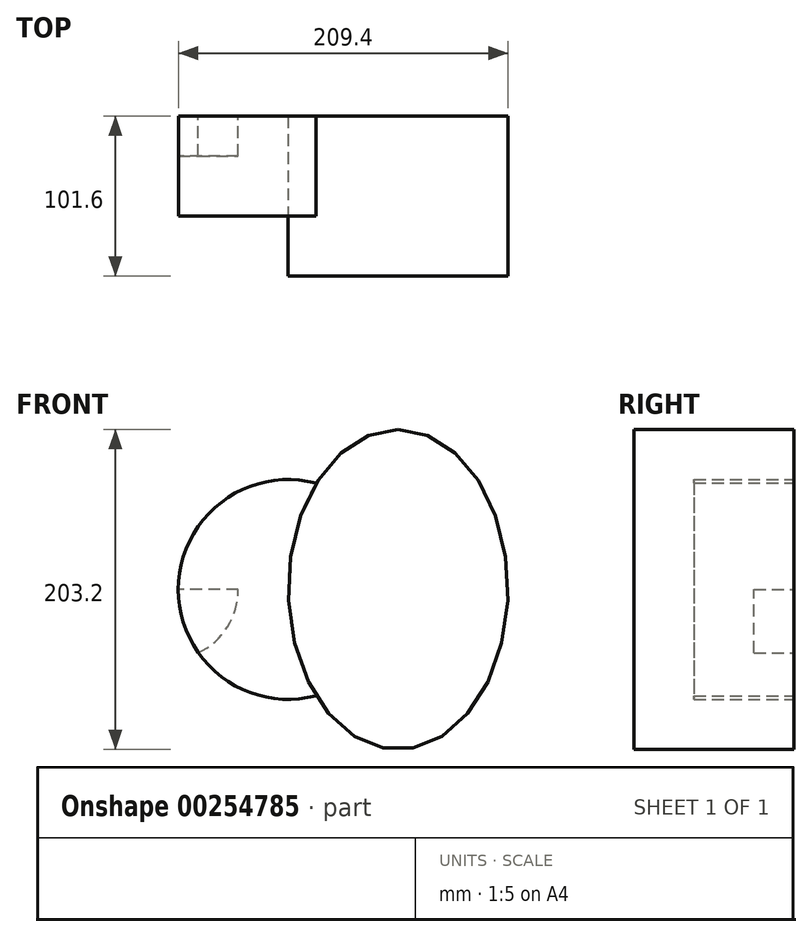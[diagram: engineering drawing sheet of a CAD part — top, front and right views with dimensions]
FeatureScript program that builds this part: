
annotation { "Feature Type Name" : "Feature", "Feature Type Description" : "" }
export const myFeature = defineFeature(function(context is Context, id is Id, definition is map)
    precondition{}
    {
        {
            var Q0;
            Q0=qCreatedBy(makeId("Front.planeOp"),FACE);
            var sketch = newSketch(context, id + "F0", { "sketchPlane" : qUnion([Q0])});
            skLineSegment(sketch, "E0", {"start": v(0, 0) * mm, "end": v(-76.2, 0) * mm});
            skCircle(sketch, "E1", {"center": v(-76.2, 0) * mm, "radius": 44.45 * mm});
            skLineSegment(sketch, "E2", {"start": v(-31.75, 0) * mm, "end": v(-69.85, 0) * mm});
            skCircle(sketch, "E3", {"center": v(0, 0) * mm, "radius": 69.8 * mm});
            skLineSegment(sketch, "E4", {"start": v(69.8, 0) * mm, "end": v(69.8, 101.6) * mm});
            skEllipse(sketch, "E5", {"center": v(69.8, 0) * mm, "majorRadius": 101.6 * mm, "minorRadius": 69.8 * mm, "majorAxis": v(0, 1)});
            skSolve(sketch);
        }
        {
            var Q0;
            {var subQ0=sQuery(id+"F0.wireOp",EDGE,"E3");var subQ1=sQuery(id+"F0.wireOp",EDGE,"E1");var subQ2=makeQuery(id+"F0.imprint","INTERSECT",VERTEX,{"disambiguationData":[OD(0.0)],"derivedFrom":[subQ1,subQ0]});Q0=makeQuery(id+"F0.imprint","IMPRINT",FACE,{"disambiguationData":[TD([[makeQuery(id+"F0.imprint","IMPRINT",EDGE,{"disambiguationData":[TD([[subQ2,-1.0]])],"derivedFrom":subQ1}),1.0]])]});}
            extrude(context, id + "F1", {"entities" : qUnion([Q0]), "depth" : 25.4 * mm});
        }
        {
            var Q0;
            {var subQ1=sQuery(id+"F0.wireOp",EDGE,"E1");var subQ3=sQuery(id+"F0.wireOp",EDGE,"E3");var subQ4=makeQuery(id+"F0.imprint","INTERSECT",VERTEX,{"disambiguationData":[OD(0.0)],"derivedFrom":[subQ1,subQ3]});Q0=makeQuery(id+"F0.imprint","IMPRINT",FACE,{"disambiguationData":[TD([[makeQuery(id+"F0.imprint","IMPRINT",EDGE,{"disambiguationData":[TD([[subQ4,-1.0]])],"derivedFrom":subQ3}),1.0]])]});}
            var Q1;
            {var subQ3=sQuery(id+"F0.wireOp",EDGE,"E1");var subQ5=sQuery(id+"F0.wireOp",EDGE,"E3");var subQ6=makeQuery(id+"F0.imprint","INTERSECT",VERTEX,{"disambiguationData":[OD(0.0)],"derivedFrom":[subQ3,subQ5]});Q1=makeQuery(id+"F0.imprint","IMPRINT",FACE,{"disambiguationData":[TD([[makeQuery(id+"F0.imprint","IMPRINT",EDGE,{"disambiguationData":[TD([[subQ6,1.0]])],"derivedFrom":subQ5}),1.0]])]});}
            var Q2;
            {var subQ3=sQuery(id+"F0.wireOp",EDGE,"E1");var subQ5=sQuery(id+"F0.wireOp",EDGE,"E3");var subQ6=makeQuery(id+"F0.imprint","INTERSECT",VERTEX,{"disambiguationData":[OD(1.0)],"derivedFrom":[subQ3,subQ5]});Q2=makeQuery(id+"F0.imprint","IMPRINT",FACE,{"disambiguationData":[TD([[makeQuery(id+"F0.imprint","IMPRINT",EDGE,{"disambiguationData":[TD([[subQ6,-1.0]])],"derivedFrom":subQ5}),1.0]])]});}
            var Q3;
            {var subQ1=sQuery(id+"F0.wireOp",EDGE,"E1");var subQ3=sQuery(id+"F0.wireOp",EDGE,"E3");var subQ4=makeQuery(id+"F0.imprint","INTERSECT",VERTEX,{"disambiguationData":[OD(1.0)],"derivedFrom":[subQ1,subQ3]});Q3=makeQuery(id+"F0.imprint","IMPRINT",FACE,{"disambiguationData":[TD([[makeQuery(id+"F0.imprint","IMPRINT",EDGE,{"disambiguationData":[TD([[subQ4,1.0]])],"derivedFrom":subQ3}),1.0]])]});}
            extrude(context, id + "F2", {"entities" : qUnion([Q0, Q1, Q2, Q3]), "depth" : 63.5 * mm});
        }
        {
            var Q0;
            {var subQ0=sQuery(id+"F0.wireOp",EDGE,"E3");var subQ1=makeQuery(id+"F0.imprint","INTERSECT",VERTEX,{"derivedFrom":[subQ0,sQuery(id+"F0.wireOp",EDGE,"E4")]});Q0=makeQuery(id+"F0.imprint","IMPRINT",FACE,{"disambiguationData":[TD([[makeQuery(id+"F0.imprint","IMPRINT",EDGE,{"disambiguationData":[TD([[subQ1,-1.0]])],"derivedFrom":subQ0}),1.0]])]});}
            var Q1;
            {var subQ0=sQuery(id+"F0.wireOp",EDGE,"E4");Q1=makeQuery(id+"F0.imprint","IMPRINT",FACE,{"disambiguationData":[TD([[makeQuery(id+"F0.imprint","IMPRINT",EDGE,{"derivedFrom":subQ0}),1.0]])]});}
            var Q2;
            {var subQ0=sQuery(id+"F0.wireOp",EDGE,"E4");Q2=makeQuery(id+"F0.imprint","IMPRINT",FACE,{"disambiguationData":[TD([[makeQuery(id+"F0.imprint","IMPRINT",EDGE,{"derivedFrom":subQ0}),-1.0]])]});}
            extrude(context, id + "F3", {"entities" : qUnion([Q0, Q1, Q2]), "depth" : 101.6 * mm});
        }
    });
